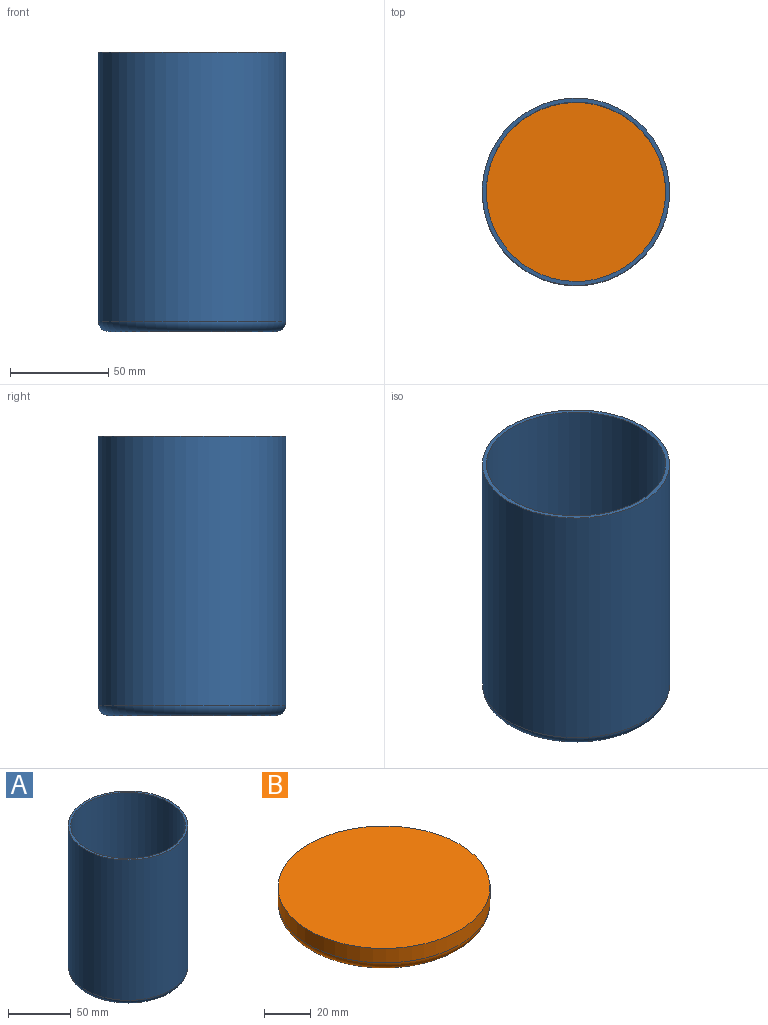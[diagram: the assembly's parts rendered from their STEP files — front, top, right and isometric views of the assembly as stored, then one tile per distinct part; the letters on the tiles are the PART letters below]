
ASSEMBLY  parts=2 mates=1
PART A: 38 faces, bbox 103x103x141.7 mm
  f0: cylinder r=47.58mm len=136.65mm, axis (0,0,1), area 40849.2mm2, adj f2,f5
  f1: plane 84.99x84.99mm, normal (0,0,-1), area 4660mm2, adj f5,f6,f7,f8,f9,f10,f11,f12
  f2: plane 95.15x95.15mm, normal (0,0,1), area 594.5mm2, adj f0,f3
  f3: cylinder r=45.54mm len=139.7mm, axis (0,0,1), area 39976.7mm2, adj f2,f4
  f4: plane 91.09x91.09mm, normal (0,0,1), area 5503mm2, adj f3,f6,f7,f8,f9,f10,f11,f12
  f5: torus R=42.5mm, axis (0,0,1), area 2292.8mm2, adj f0,f1
  f6: cylinder r=3.17mm len=6.35mm, axis (0,0,-1), area 40.5mm2, adj f1,f4
  f7: cylinder r=3.17mm len=6.35mm, axis (0,0,-1), area 40.5mm2, adj f1,f4
  f8: cylinder r=3.17mm len=6.35mm, axis (0,0,-1), area 40.5mm2, adj f1,f4
  f9: cylinder r=3.17mm len=6.35mm, axis (0,0,-1), area 40.5mm2, adj f1,f4
  f10: cylinder r=3.17mm len=6.35mm, axis (0,0,-1), area 40.5mm2, adj f1,f4
  f11: cylinder r=3.17mm len=6.35mm, axis (0,0,-1), area 40.5mm2, adj f1,f4
  f12: cylinder r=3.17mm len=6.35mm, axis (0,0,-1), area 40.5mm2, adj f1,f4
  f13: cylinder r=3.17mm len=6.35mm, axis (0,0,-1), area 40.5mm2, adj f1,f4
  f14: cylinder r=3.17mm len=6.35mm, axis (0,0,-1), area 40.5mm2, adj f1,f4
  f15: cylinder r=3.17mm len=6.35mm, axis (0,0,-1), area 40.5mm2, adj f1,f4
  f16: cylinder r=3.17mm len=6.35mm, axis (0,0,-1), area 40.5mm2, adj f1,f4
  f17: cylinder r=3.17mm len=6.35mm, axis (0,0,-1), area 40.5mm2, adj f1,f4
  f18: cylinder r=3.17mm len=6.35mm, axis (0,0,-1), area 40.5mm2, adj f1,f4
  f19: cylinder r=3.17mm len=6.35mm, axis (0,0,-1), area 40.5mm2, adj f1,f4
  f20: cylinder r=3.17mm len=6.35mm, axis (0,0,-1), area 40.5mm2, adj f1,f4
  f21: cylinder r=3.17mm len=6.35mm, axis (0,0,-1), area 40.5mm2, adj f1,f4
  f22: cylinder r=3.17mm len=6.35mm, axis (0,0,-1), area 40.5mm2, adj f1,f4
  f23: cylinder r=3.17mm len=6.35mm, axis (0,0,-1), area 40.5mm2, adj f1,f4
  f24: cylinder r=3.17mm len=6.35mm, axis (0,0,-1), area 40.5mm2, adj f1,f4
  f25: cylinder r=3.17mm len=6.35mm, axis (0,0,-1), area 40.5mm2, adj f1,f4
  f26: cylinder r=3.17mm len=6.35mm, axis (0,0,-1), area 40.5mm2, adj f1,f4
  f27: cylinder r=3.17mm len=6.35mm, axis (0,0,-1), area 40.5mm2, adj f1,f4
  f28: cylinder r=3.17mm len=6.35mm, axis (0,0,-1), area 40.5mm2, adj f1,f4
  f29: cylinder r=3.17mm len=6.35mm, axis (0,0,-1), area 40.5mm2, adj f1,f4
  f30: cylinder r=3.17mm len=6.35mm, axis (0,0,-1), area 40.5mm2, adj f1,f4
  f31: cylinder r=3.17mm len=6.35mm, axis (0,0,-1), area 40.5mm2, adj f1,f4
  f32: cylinder r=3.17mm len=6.35mm, axis (0,0,-1), area 40.5mm2, adj f1,f4
  f33: cylinder r=3.17mm len=6.35mm, axis (0,0,-1), area 40.5mm2, adj f1,f4
  f34: cylinder r=3.17mm len=6.35mm, axis (0,0,-1), area 40.5mm2, adj f1,f4
  f35: cylinder r=3.17mm len=6.35mm, axis (0,0,-1), area 40.5mm2, adj f1,f4
  f36: cylinder r=3.17mm len=6.35mm, axis (0,0,-1), area 40.5mm2, adj f1,f4
  f37: cylinder r=3.17mm len=6.35mm, axis (0,0,-1), area 40.5mm2, adj f1,f4
PART B: 4 faces, bbox 98.6x98.6x12.7 mm
  f0: cylinder r=45.54mm len=91.09mm, axis (0,0,1), area 2180.5mm2, adj f2,f3
  f1: plane 80.93x80.93mm, normal (0,0,-1), area 5143.8mm2, adj f3
  f2: plane 91.09x91.09mm, normal (0,0,1), area 6516.4mm2, adj f0
  f3: torus R=40.46mm, axis (0,0,1), area 2190.9mm2, adj f0,f1
PLACE A t=(-85.26,-21.26,-125.79)mm
PLACE B t=(-85.26,-21.26,-252.79)mm
MATE cylindrical B.f0 <-> A.f0  axis (0,0,-1) through (-85.26,-21.26,-265.49)mm
